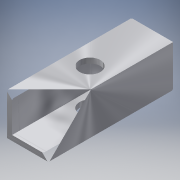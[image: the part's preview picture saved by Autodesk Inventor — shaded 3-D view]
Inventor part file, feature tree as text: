
AUTODESK INVENTOR PART (.ipt)
format: ipt  version: 2016 (Build 200138000, 138)  size: 112,640 bytes
history: native  units: in
note: dims shown in document units (in); Inventor stores cm internally (conversion verified against a paired STEP export)
features: sketch x2, extrude x1, hole x1
ambient origin geometry x8: Origin, YZ Plane, XZ Plane, XY Plane, X Axis, Y Axis, Z Axis, Center Point
bodies: Solid1 (feature_tree)
feature tree (4):
  extrude  "Extrusion1"  Depth=1.0in
  hole  "Hole1"  [1 undecoded]
  sketch  "Sketch1"  dims[d0=1.0in d1=1.0in]
  sketch  "Sketch2"  dims[d2=0.125in d3=3.0in d4=0.0in d5=0.5in d6=1.5in d7=0.5in d8=0.75in d9=0.375in d10=0.25in d11=0.5635in d12=1.0in d13=0.8108in]
note: 1 required parameter value undecoded (feature->parameter linkage not recoverable at this tier; creation-order binding heuristic only, values carry confidence <= 0.55)
